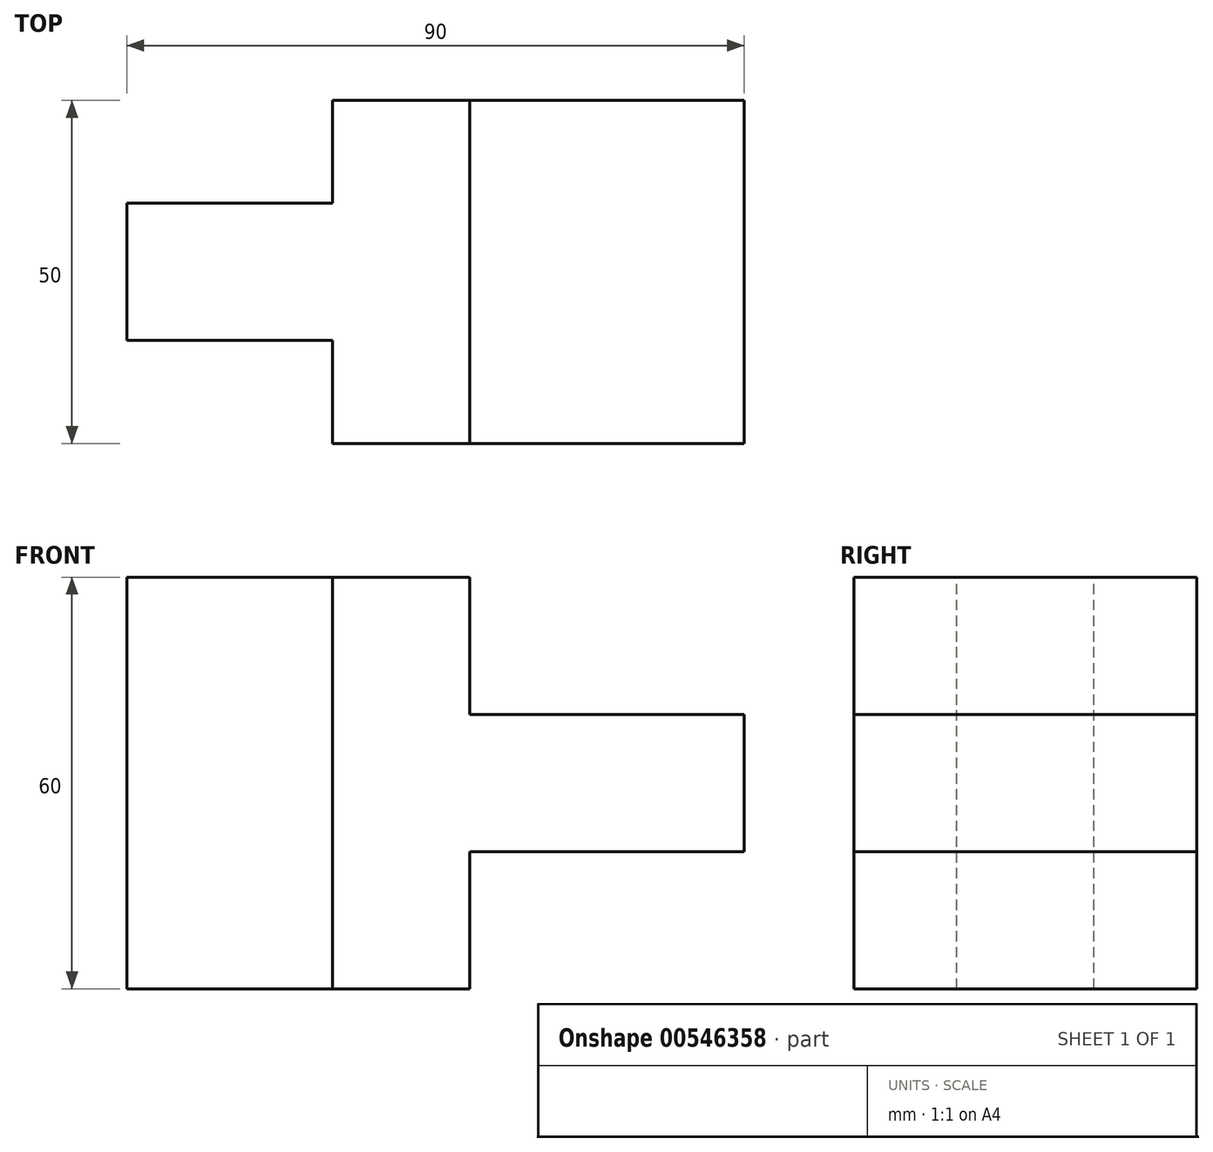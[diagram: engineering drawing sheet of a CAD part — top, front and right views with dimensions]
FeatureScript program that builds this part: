
annotation { "Feature Type Name" : "Feature", "Feature Type Description" : "" }
export const myFeature = defineFeature(function(context is Context, id is Id, definition is map)
    precondition{}
    {
        {
            var Q0;
            Q0=qCreatedBy(makeId("Front.planeOp"),FACE);
            var sketch = newSketch(context, id + "F0", { "sketchPlane" : qUnion([Q0])});
            skLineSegment(sketch, "E0.bottom", {"start": v(45, -30) * mm, "end": v(-45, -30) * mm});
            skLineSegment(sketch, "E0.top", {"start": v(45, 30) * mm, "end": v(-45, 30) * mm});
            skLineSegment(sketch, "E0.left", {"start": v(45, -30) * mm, "end": v(45, 30) * mm});
            skLineSegment(sketch, "E0.right", {"start": v(-45, -30) * mm, "end": v(-45, 30) * mm});
            skPoint(sketch, "E0.middle", {"position": v(0, 0) * mm});
            skSolve(sketch);
        }
        {
            var Q0;
            Q0 = qSketchRegion(id + "F0", true);
            extrude(context, id + "F1", {"entities" : qUnion([Q0]), "depth" : 50 * mm, "offsetDistance" : 25 * mm});
        }
        {
            var Q0;
            Q0=makeQuery(id+"F1.opExtrude","CAP_FACE",FACE,{"disambiguationData":[OSD([sQuery(id+"F0.wireOp",EDGE,"E0.bottom"),sQuery(id+"F0.wireOp",EDGE,"E0.top"),sQuery(id+"F0.wireOp",EDGE,"E0.left"),sQuery(id+"F0.wireOp",EDGE,"E0.right")])],"isStart":false});
            var sketch = newSketch(context, id + "F2", { "sketchPlane" : qUnion([Q0])});
            skLineSegment(sketch, "E1", {"start": v(45, -10) * mm, "end": v(5, -10) * mm});
            skLineSegment(sketch, "E2", {"start": v(5, -10) * mm, "end": v(5, -30) * mm});
            skLineSegment(sketch, "E3", {"start": v(45, 10) * mm, "end": v(5, 10) * mm});
            skLineSegment(sketch, "E4", {"start": v(5, 10) * mm, "end": v(5, 30) * mm});
            skLineSegment(sketch, "E5", {"start": v(-15, 30) * mm, "end": v(-15, -30) * mm});
            skSolve(sketch);
        }
        {
            var Q0;
            {var subQ0=sQuery(id+"F2.wireOp",EDGE,"E3");Q0=makeQuery(id+"F2.imprint","IMPRINT",FACE,{"disambiguationData":[TD([[makeQuery(id+"F2.imprint","IMPRINT",EDGE,{"derivedFrom":subQ0}),-1.0]])]});}
            extrude(context, id + "F3", {"entities" : qUnion([Q0]), "operationType" : NewBodyOperationType.REMOVE, "endBound" : BoundingType.THROUGH_ALL, "oppositeDirection" : true, "depth" : 25 * mm, "offsetDistance" : 25 * mm});
        }
        {
            var Q0;
            {var subQ0=sQuery(id+"F2.wireOp",EDGE,"E1");Q0=makeQuery(id+"F2.imprint","IMPRINT",FACE,{"disambiguationData":[TD([[makeQuery(id+"F2.imprint","IMPRINT",EDGE,{"derivedFrom":subQ0}),1.0]])]});}
            extrude(context, id + "F4", {"entities" : qUnion([Q0]), "operationType" : NewBodyOperationType.REMOVE, "endBound" : BoundingType.THROUGH_ALL, "oppositeDirection" : true, "depth" : 25 * mm, "offsetDistance" : 25 * mm});
        }
        {
            var Q0;
            Q0=makeQuery(id+"F1.opExtrude","SWEPT_FACE",FACE,{"disambiguationData":[OSD([sQuery(id+"F0.wireOp",EDGE,"E0.top")])]});
            var sketch = newSketch(context, id + "F5", { "sketchPlane" : qUnion([Q0])});
            skLineSegment(sketch, "E6", {"start": v(-15, 0) * mm, "end": v(-15, -15) * mm});
            skLineSegment(sketch, "E7", {"start": v(-15, -15) * mm, "end": v(-45, -15) * mm});
            skLineSegment(sketch, "E8", {"start": v(-15, -50) * mm, "end": v(-15, -35) * mm});
            skLineSegment(sketch, "E9", {"start": v(-15, -35) * mm, "end": v(-45, -35) * mm});
            skSolve(sketch);
        }
        {
            var Q0;
            {var subQ0=sQuery(id+"F5.wireOp",EDGE,"E6");Q0=makeQuery(id+"F5.imprint","IMPRINT",FACE,{"disambiguationData":[TD([[makeQuery(id+"F5.imprint","IMPRINT",EDGE,{"derivedFrom":subQ0}),-1.0]])]});}
            var Q1;
            {var subQ0=sQuery(id+"F5.wireOp",EDGE,"E8");Q1=makeQuery(id+"F5.imprint","IMPRINT",FACE,{"disambiguationData":[TD([[makeQuery(id+"F5.imprint","IMPRINT",EDGE,{"derivedFrom":subQ0}),1.0]])]});}
            extrude(context, id + "F6", {"entities" : qUnion([Q0, Q1]), "operationType" : NewBodyOperationType.REMOVE, "endBound" : BoundingType.THROUGH_ALL, "oppositeDirection" : true, "depth" : 25 * mm, "offsetDistance" : 25 * mm});
        }
    });
